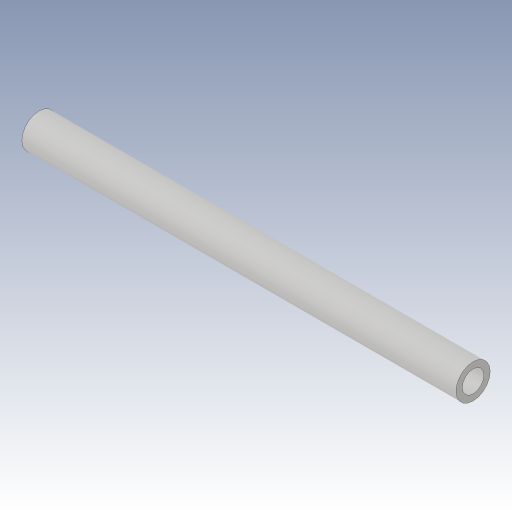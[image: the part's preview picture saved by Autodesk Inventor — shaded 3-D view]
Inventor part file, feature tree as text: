
AUTODESK INVENTOR PART (.ipt)
format: ipt  version: 2023.3 (Build 273359000, 359)  size: 118,784 bytes
history: native  units: in
note: dims shown in document units (in); Inventor stores cm internally (conversion verified against a paired STEP export)
features: extrude x1, sketch x1
ambient origin geometry x8: Origin, YZ Plane, XZ Plane, XY Plane, X Axis, Y Axis, Z Axis, Center Point
bodies: Body1 (feature_tree)
feature tree (2):
  extrude  "Extrusion3"  Depth=0.5512in
  sketch  "Skizze3"  dims[d4=0.0276in d5=0.0433in d6=0.5512in d7=0.0in]
